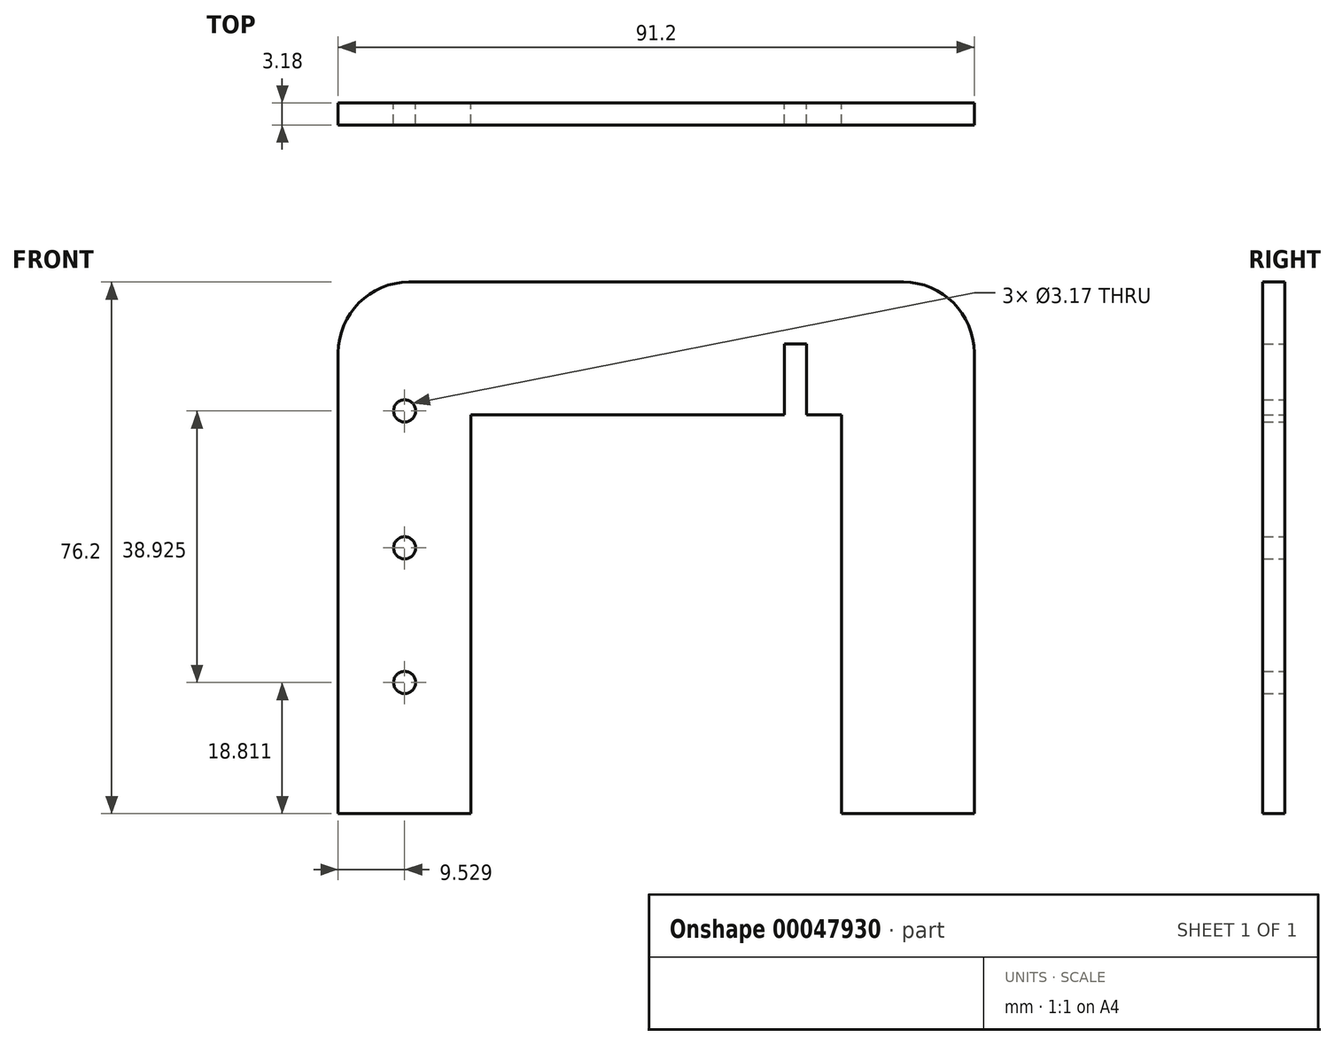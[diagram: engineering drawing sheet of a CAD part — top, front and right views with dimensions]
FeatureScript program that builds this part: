
annotation { "Feature Type Name" : "Feature", "Feature Type Description" : "" }
export const myFeature = defineFeature(function(context is Context, id is Id, definition is map)
    precondition{}
    {
        {
            var Q0;
            Q0=qCreatedBy(makeId("Front.planeOp"),FACE);
            var sketch = newSketch(context, id + "F0", { "sketchPlane" : qUnion([Q0])});
            skLineSegment(sketch, "E0.bottom", {"start": v(-45.7, -49.45) * mm, "end": v(-26.65, -49.45) * mm});
            skLineSegment(sketch, "E0.top", {"start": v(-45.7, 26.75) * mm, "end": v(-36.81, 26.75) * mm});
            skLineSegment(sketch, "E0.left", {"start": v(-45.7, -49.45) * mm, "end": v(-45.7, 7.7) * mm});
            skLineSegment(sketch, "E0.right", {"start": v(-26.65, -49.45) * mm, "end": v(-26.65, 16.6) * mm});
            skLineSegment(sketch, "E1.bottom", {"start": v(-45.7, 26.75) * mm, "end": v(-107.69, 26.75) * mm});
            skLineSegment(sketch, "E1.top", {"start": v(-45.7, 7.7) * mm, "end": v(-50.66, 7.7) * mm});
            skLineSegment(sketch, "E1.right", {"start": v(-117.85, 16.6) * mm, "end": v(-117.85, 7.7) * mm});
            skLineSegment(sketch, "E2.top", {"start": v(-117.85, -49.45) * mm, "end": v(-98.8, -49.45) * mm});
            skLineSegment(sketch, "E2.left", {"start": v(-117.85, 7.7) * mm, "end": v(-117.85, -49.45) * mm});
            skLineSegment(sketch, "E2.right", {"start": v(-98.8, 7.7) * mm, "end": v(-98.8, -49.45) * mm});
            skCircle(sketch, "E3", {"center": v(-108.32, 8.29) * mm, "radius": 1.59 * mm});
            skCircle(sketch, "E4", {"center": v(-108.32, -11.35) * mm, "radius": 1.59 * mm});
            skCircle(sketch, "E5", {"center": v(-108.32, -30.64) * mm, "radius": 1.59 * mm});
            skCircle(sketch, "E6", {"center": v(-51.17, -30.64) * mm, "radius": 1.59 * mm});
            skPoint(sketch, "E7.visualSharp", {"position": v(-117.85, 26.75) * mm});
            skArc(sketch, "E7.filletArc", {"start": v(-107.69, 26.75) * mm, "mid": v(-114.87, 23.78) * mm, "end": v(-117.85, 16.6) * mm});
            skPoint(sketch, "E8.visualSharp", {"position": v(-26.65, 26.75) * mm});
            skArc(sketch, "E8.filletArc", {"start": v(-26.65, 16.6) * mm, "mid": v(-29.63, 23.78) * mm, "end": v(-36.81, 26.75) * mm});
            skLineSegment(sketch, "E9.left", {"start": v(-117.57, 18.95) * mm, "end": v(-117.57, 15.77) * mm});
            skLineSegment(sketch, "E10", {"start": v(-53.84, 7.7) * mm, "end": v(-53.84, 17.86) * mm});
            skLineSegment(sketch, "E11", {"start": v(-53.84, 17.86) * mm, "end": v(-50.66, 17.86) * mm});
            skLineSegment(sketch, "E12", {"start": v(-50.66, 17.86) * mm, "end": v(-50.66, 7.7) * mm});
            skLineSegment(sketch, "E13.trimOffspring", {"start": v(-53.84, 7.7) * mm, "end": v(-98.8, 7.7) * mm});
            skSolve(sketch);
        }
        {
            var Q0;
            Q0=makeQuery(id+"F0.imprint","IMPRINT",FACE,{"disambiguationData":[TD([[makeQuery(id+"F0.imprint","IMPRINT",EDGE,{"derivedFrom":sQuery(id+"F0.wireOp",EDGE,"E0.bottom")}),1.0]])]});
            extrude(context, id + "F1", {"entities" : qUnion([Q0]), "depth" : 3.17 * mm});
        }
    });
